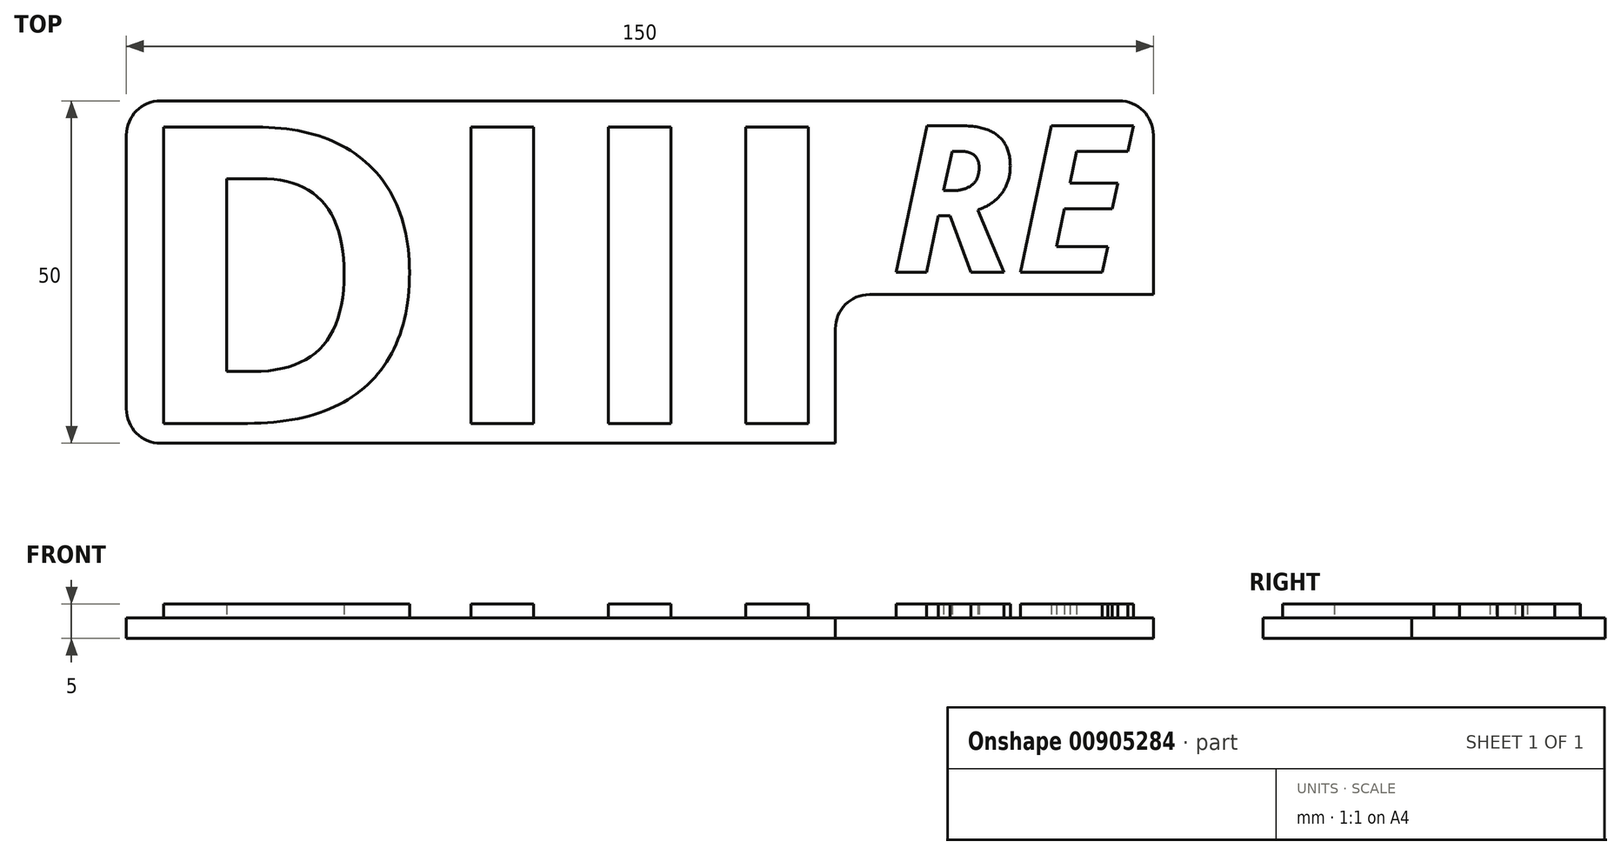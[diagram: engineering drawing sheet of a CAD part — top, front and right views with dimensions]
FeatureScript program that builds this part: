
annotation { "Feature Type Name" : "Feature", "Feature Type Description" : "" }
export const myFeature = defineFeature(function(context is Context, id is Id, definition is map)
    precondition{}
    {
        {
            var Q0;
            Q0=qCreatedBy(makeId("Top.planeOp"),FACE);
            var sketch = newSketch(context, id + "F0", { "sketchPlane" : qUnion([Q0])});
            skLineSegment(sketch, "E0.bottom", {"start": v(75, -25) * mm, "end": v(-75, -25) * mm});
            skLineSegment(sketch, "E0.top", {"start": v(75, 25) * mm, "end": v(-75, 25) * mm});
            skLineSegment(sketch, "E0.left", {"start": v(75, -25) * mm, "end": v(75, 25) * mm});
            skLineSegment(sketch, "E0.right", {"start": v(-75, -25) * mm, "end": v(-75, 25) * mm});
            skPoint(sketch, "E0.middle", {"position": v(28.55, 0) * mm});
            skText(sketch, "E1", { "text": "DIII", "fontName": "OpenSans-Bold.ttf"});
            skText(sketch, "E2", { "text": "RE", "fontName": "OpenSans-BoldItalic.ttf"});
            const initialGuessF0  = {"E1": [-0.075, -0.0221, 1, 0, 0.04364], "E2": [0.03663, 0, 1, 0, 0.02154]};
            skSetInitialGuess(sketch, initialGuessF0);
            skSolve(sketch);
        }
        {
            var Q0;
            Q0=makeQuery(id+"F0.imprint","IMPRINT",FACE,{"disambiguationData":[TD([[makeQuery(id+"F0.imprint","IMPRINT",EDGE,{"derivedFrom":sQuery(id+"F0.wireOp",EDGE,"E2.sketch_text.stroke-0")}),-1.0]])]});
            var Q1;
            Q1=makeQuery(id+"F0.imprint","IMPRINT",FACE,{"disambiguationData":[TD([[makeQuery(id+"F0.imprint","IMPRINT",EDGE,{"derivedFrom":sQuery(id+"F0.wireOp",EDGE,"E0.bottom")}),-1.0]])]});
            var Q2;
            Q2=makeQuery(id+"F0.imprint","IMPRINT",FACE,{"disambiguationData":[TD([[makeQuery(id+"F0.imprint","IMPRINT",EDGE,{"derivedFrom":sQuery(id+"F0.wireOp",EDGE,"E2.sketch_text.stroke-19")}),-1.0]])]});
            var Q3;
            Q3=makeQuery(id+"F0.imprint","IMPRINT",FACE,{"disambiguationData":[TD([[makeQuery(id+"F0.imprint","IMPRINT",EDGE,{"derivedFrom":sQuery(id+"F0.wireOp",EDGE,"E2.sketch_text.stroke-0")}),1.0]])]});
            var Q4;
            Q4=makeQuery(id+"F0.imprint","IMPRINT",FACE,{"disambiguationData":[TD([[makeQuery(id+"F0.imprint","IMPRINT",EDGE,{"derivedFrom":sQuery(id+"F0.wireOp",EDGE,"E1.sketch_text.stroke-20")}),-1.0]])]});
            var Q5;
            Q5=makeQuery(id+"F0.imprint","IMPRINT",FACE,{"disambiguationData":[TD([[makeQuery(id+"F0.imprint","IMPRINT",EDGE,{"derivedFrom":sQuery(id+"F0.wireOp",EDGE,"E1.sketch_text.stroke-16")}),-1.0]])]});
            var Q6;
            Q6=makeQuery(id+"F0.imprint","IMPRINT",FACE,{"disambiguationData":[TD([[makeQuery(id+"F0.imprint","IMPRINT",EDGE,{"derivedFrom":sQuery(id+"F0.wireOp",EDGE,"E1.sketch_text.stroke-12")}),-1.0]])]});
            var Q7;
            Q7=makeQuery(id+"F0.imprint","IMPRINT",FACE,{"disambiguationData":[TD([[makeQuery(id+"F0.imprint","IMPRINT",EDGE,{"derivedFrom":sQuery(id+"F0.wireOp",EDGE,"E1.sketch_text.stroke-7")}),1.0]])]});
            var Q8;
            Q8=makeQuery(id+"F0.imprint","IMPRINT",FACE,{"disambiguationData":[TD([[makeQuery(id+"F0.imprint","IMPRINT",EDGE,{"derivedFrom":sQuery(id+"F0.wireOp",EDGE,"E1.sketch_text.stroke-0")}),-1.0]])]});
            extrude(context, id + "F1", {"entities" : qUnion([Q0, Q1, Q2, Q3, Q4, Q5, Q6, Q7, Q8]), "depth" : 3 * mm, "offsetDistance" : 25 * mm});
        }
        {
            var Q0;
            Q0=makeQuery(id+"F0.imprint","IMPRINT",FACE,{"disambiguationData":[TD([[makeQuery(id+"F0.imprint","IMPRINT",EDGE,{"derivedFrom":sQuery(id+"F0.wireOp",EDGE,"E1.sketch_text.stroke-0")}),-1.0]])]});
            var Q1;
            Q1=makeQuery(id+"F0.imprint","IMPRINT",FACE,{"disambiguationData":[TD([[makeQuery(id+"F0.imprint","IMPRINT",EDGE,{"derivedFrom":sQuery(id+"F0.wireOp",EDGE,"E1.sketch_text.stroke-12")}),-1.0]])]});
            var Q2;
            Q2=makeQuery(id+"F0.imprint","IMPRINT",FACE,{"disambiguationData":[TD([[makeQuery(id+"F0.imprint","IMPRINT",EDGE,{"derivedFrom":sQuery(id+"F0.wireOp",EDGE,"E1.sketch_text.stroke-16")}),-1.0]])]});
            var Q3;
            Q3=makeQuery(id+"F0.imprint","IMPRINT",FACE,{"disambiguationData":[TD([[makeQuery(id+"F0.imprint","IMPRINT",EDGE,{"derivedFrom":sQuery(id+"F0.wireOp",EDGE,"E1.sketch_text.stroke-20")}),-1.0]])]});
            var Q4;
            Q4=makeQuery(id+"F0.imprint","IMPRINT",FACE,{"disambiguationData":[TD([[makeQuery(id+"F0.imprint","IMPRINT",EDGE,{"derivedFrom":sQuery(id+"F0.wireOp",EDGE,"E2.sketch_text.stroke-0")}),-1.0]])]});
            var Q5;
            Q5=makeQuery(id+"F0.imprint","IMPRINT",FACE,{"disambiguationData":[TD([[makeQuery(id+"F0.imprint","IMPRINT",EDGE,{"derivedFrom":sQuery(id+"F0.wireOp",EDGE,"E2.sketch_text.stroke-19")}),-1.0]])]});
            extrude(context, id + "F2", {"entities" : qUnion([Q0, Q1, Q2, Q3, Q4, Q5]), "operationType" : NewBodyOperationType.ADD, "depth" : 5 * mm, "offsetDistance" : 25 * mm});
        }
        {
            var Q0;
            {var subQ0=sQuery(id+"F0.wireOp",EDGE,"E0.bottom");var subQ1=sQuery(id+"F0.wireOp",EDGE,"E0.right");var subQ2=sQuery(id+"F0.wireOp",EDGE,"E0.left");var subQ3=sQuery(id+"F0.wireOp",EDGE,"E0.top");Q0=makeQuery(id+"F2.boolean.opBoolean","SPLIT",FACE,{"disambiguationData":[TD([makeQuery(id+"F1.opExtrude","SWEPT_FACE",FACE,{"disambiguationData":[OSD([subQ0])]})])],"derivedFrom":makeQuery(id+"F1.opExtrude","CAP_FACE",FACE,{"disambiguationData":[OSD([subQ0,subQ3,subQ2,subQ1])],"isStart":false})});}
            var sketch = newSketch(context, id + "F3", { "sketchPlane" : qUnion([Q0])});
            skLineSegment(sketch, "E3.0", {"start": v(75, -25) * mm, "end": v(-75, -25) * mm});
            skLineSegment(sketch, "E3.1", {"start": v(75, 25) * mm, "end": v(-75, 25) * mm});
            skLineSegment(sketch, "E3.2", {"start": v(75, -25) * mm, "end": v(75, 25) * mm});
            skLineSegment(sketch, "E3.3", {"start": v(-75, -25) * mm, "end": v(-75, 25) * mm});
            skPoint(sketch, "E3.4", {"position": v(28.55, 0) * mm});
            skLineSegment(sketch, "E4", {"start": v(48.35, 0) * mm, "end": v(48.35, -3.28) * mm, "construction": true});
            skLineSegment(sketch, "E5", {"start": v(48.35, -3.28) * mm, "end": v(28.55, -3.28) * mm});
            skLineSegment(sketch, "E6", {"start": v(48.35, -3.28) * mm, "end": v(75, -3.28) * mm});
            skLineSegment(sketch, "E7", {"start": v(28.55, -3.28) * mm, "end": v(28.55, -25) * mm});
            skLineSegment(sketch, "E8", {"start": v(28.55, -25) * mm, "end": v(75, -25) * mm});
            skSolve(sketch);
        }
        {
            var Q0;
            Q0=makeQuery(id+"F3.imprint","IMPRINT",FACE,{"disambiguationData":[TD([[makeQuery(id+"F3.imprint","IMPRINT",EDGE,{"derivedFrom":sQuery(id+"F3.wireOp",EDGE,"E5")}),1.0]])]});
            extrude(context, id + "F4", {"entities" : qUnion([Q0]), "operationType" : NewBodyOperationType.REMOVE, "oppositeDirection" : true, "depth" : 6 * mm, "offsetDistance" : 25 * mm});
        }
        {
            var Q0;
            Q0=makeQuery(id+"F4.boolean.opBoolean","COPY",EDGE,{"derivedFrom":makeQuery(id+"F4.opExtrude","SWEPT_EDGE",EDGE,{"disambiguationData":[OSD([sQuery(id+"F3.wireOp",EDGE,"E5"),sQuery(id+"F3.wireOp",EDGE,"E7")])]})});
            var Q1;
            Q1=makeQuery(id+"F4.boolean.opBoolean","COPY",EDGE,{"derivedFrom":makeQuery(id+"F4.opExtrude","SWEPT_EDGE",EDGE,{"disambiguationData":[OSD([sQuery(id+"F3.wireOp",EDGE,"E3.0"),sQuery(id+"F3.wireOp",EDGE,"E7"),sQuery(id+"F3.wireOp",EDGE,"E8")])]})});
            var Q2;
            Q2=makeQuery(id+"F4.boolean.opBoolean","COPY",EDGE,{"derivedFrom":makeQuery(id+"F4.opExtrude","SWEPT_EDGE",EDGE,{"disambiguationData":[OSD([sQuery(id+"F3.wireOp",EDGE,"E3.2"),sQuery(id+"F3.wireOp",EDGE,"E6")])]})});
            var Q3;
            Q3=makeQuery(id+"F1.opExtrude","SWEPT_EDGE",EDGE,{"disambiguationData":[OSD([sQuery(id+"F0.wireOp",EDGE,"E0.top"),sQuery(id+"F0.wireOp",EDGE,"E0.left")])]});
            var Q4;
            Q4=makeQuery(id+"F1.opExtrude","SWEPT_EDGE",EDGE,{"disambiguationData":[OSD([sQuery(id+"F0.wireOp",EDGE,"E0.bottom"),sQuery(id+"F0.wireOp",EDGE,"E0.right")])]});
            var Q5;
            Q5=makeQuery(id+"F1.opExtrude","SWEPT_EDGE",EDGE,{"disambiguationData":[OSD([sQuery(id+"F0.wireOp",EDGE,"E0.top"),sQuery(id+"F0.wireOp",EDGE,"E0.right")])]});
            fillet(context, id + "F5", {"entities" : qUnion([Q0, Q1, Q2, Q3, Q4, Q5]), "radius" : 5 * mm, "tangentPropagation" : true, "allowEdgeOverflow" : false});
        }
    });
